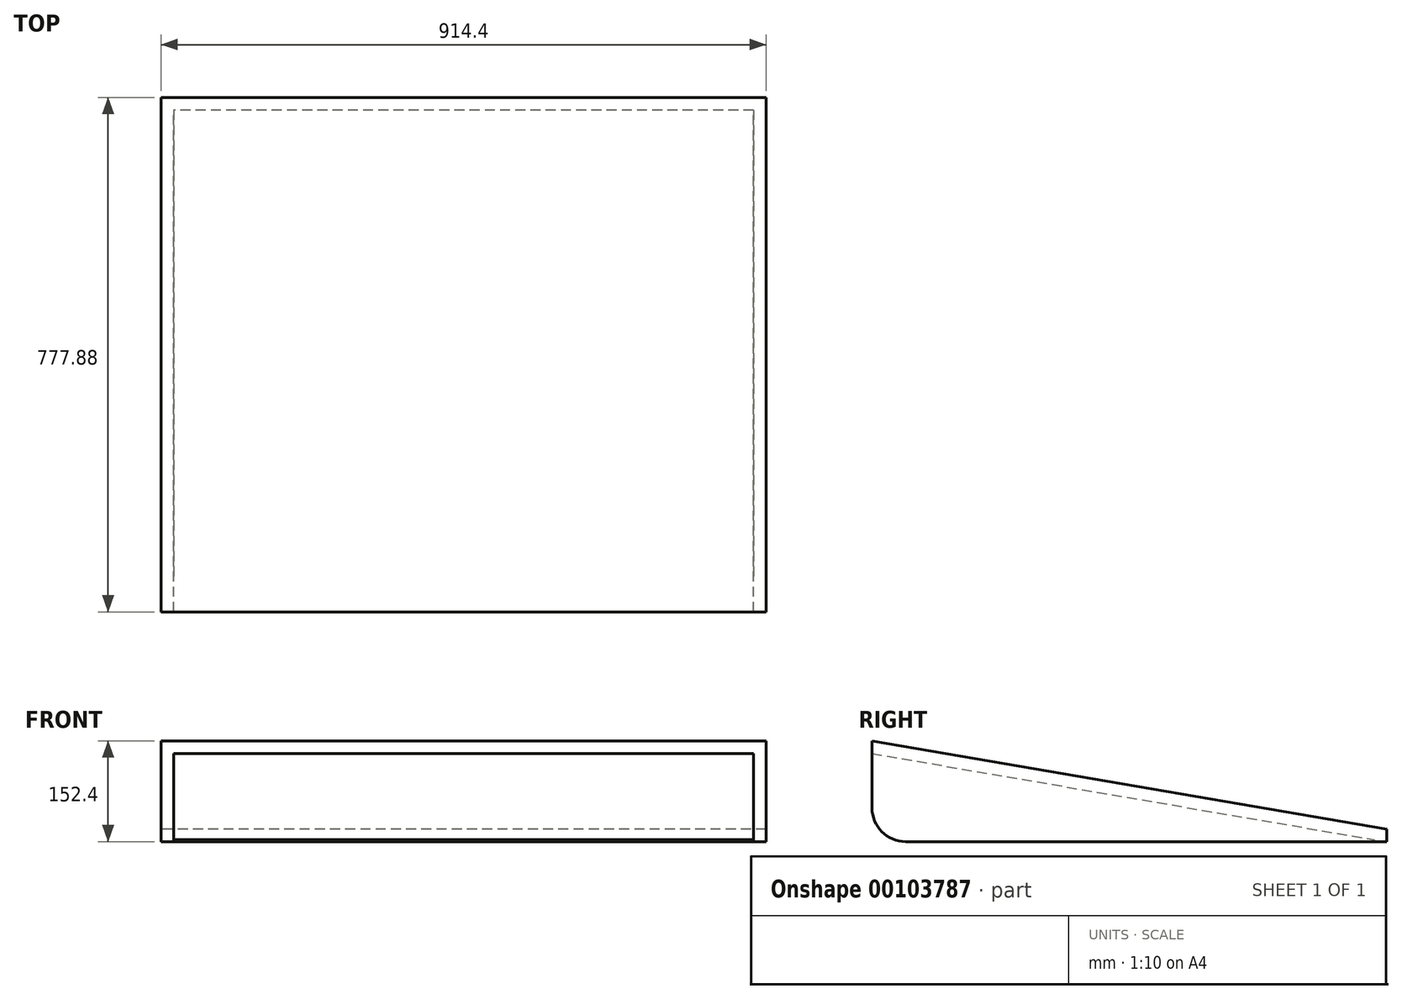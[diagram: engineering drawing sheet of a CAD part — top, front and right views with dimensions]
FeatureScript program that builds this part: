
annotation { "Feature Type Name" : "Feature", "Feature Type Description" : "" }
export const myFeature = defineFeature(function(context is Context, id is Id, definition is map)
    precondition{}
    {
        {
            var Q0;
            Q0=qCreatedBy(makeId("Right.planeOp"),FACE);
            var sketch = newSketch(context, id + "F0", { "sketchPlane" : qUnion([Q0])});
            skLineSegment(sketch, "E0", {"start": v(0, 0) * mm, "end": v(-111.12, 0) * mm, "construction": true});
            skLineSegment(sketch, "E1", {"start": v(-889, 50.8) * mm, "end": v(-889, 152.4) * mm});
            skLineSegment(sketch, "E2", {"start": v(-889, 152.4) * mm, "end": v(-111.12, 19.05) * mm});
            skPoint(sketch, "E3.visualSharp", {"position": v(-889, 0) * mm});
            skArc(sketch, "E3.filletArc", {"start": v(-889, 50.8) * mm, "mid": v(-874.12, 14.88) * mm, "end": v(-838.2, 0) * mm});
            skLineSegment(sketch, "E4", {"start": v(-111.12, 19.05) * mm, "end": v(-111.12, 0) * mm});
            skLineSegment(sketch, "E5", {"start": v(-111.12, 19.05) * mm, "end": v(0, 0) * mm, "construction": true});
            skLineSegment(sketch, "E6", {"start": v(-111.12, 0) * mm, "end": v(-838.2, 0) * mm});
            skSolve(sketch);
        }
        {
            var Q0;
            Q0 = qSketchRegion(id + "F0", true);
            extrude(context, id + "F1", {"entities" : qUnion([Q0]), "depth" : 914.4 * mm});
        }
        {
            var Q0;
            Q0=makeQuery(id+"F1.opExtrude","SWEPT_FACE",FACE,{"disambiguationData":[OSD([sQuery(id+"F0.wireOp",EDGE,"E6")])]});
            var Q1;
            Q1=makeQuery(id+"F1.opExtrude","SWEPT_FACE",FACE,{"disambiguationData":[OSD([sQuery(id+"F0.wireOp",EDGE,"E3.filletArc")])]});
            var Q2;
            Q2=makeQuery(id+"F1.opExtrude","SWEPT_FACE",FACE,{"disambiguationData":[OSD([sQuery(id+"F0.wireOp",EDGE,"E1")])]});
            shell(context, id + "F2", {"entities" : qUnion([Q0, Q1, Q2]), "thickness" : 19.05 * mm});
        }
    });
